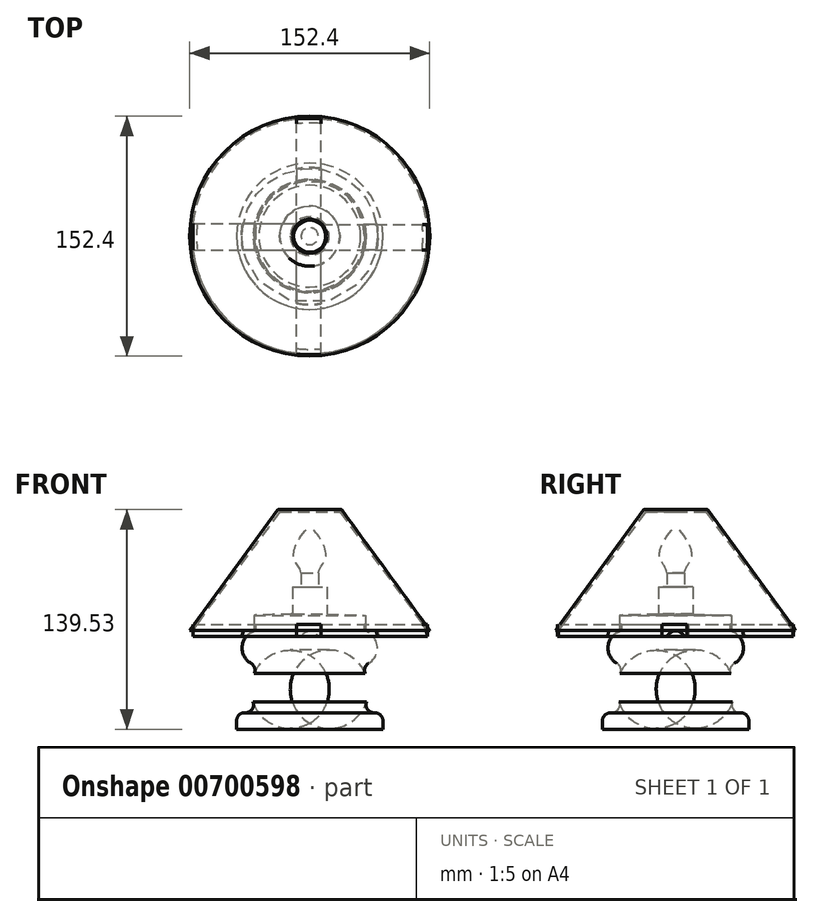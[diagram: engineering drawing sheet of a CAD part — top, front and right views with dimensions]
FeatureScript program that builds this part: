
annotation { "Feature Type Name" : "Feature", "Feature Type Description" : "" }
export const myFeature = defineFeature(function(context is Context, id is Id, definition is map)
    precondition{}
    {
        {
            var Q0;
            Q0=qCreatedBy(makeId("Front.planeOp"),FACE);
            var sketch = newSketch(context, id + "F0", { "sketchPlane" : qUnion([Q0])});
            skLineSegment(sketch, "E0", {"start": v(-76.2, 0) * mm, "end": v(-20.32, 76.66) * mm});
            skLineSegment(sketch, "E1", {"start": v(-20.32, 76.66) * mm, "end": v(0, 77.04) * mm});
            skLineSegment(sketch, "E2", {"start": v(0, 77.04) * mm, "end": v(0, -62.86) * mm});
            skLineSegment(sketch, "E3", {"start": v(0, -62.86) * mm, "end": v(-46.45, -62.86) * mm});
            skLineSegment(sketch, "E4", {"start": v(-46.45, -62.86) * mm, "end": v(-46.45, -52.2) * mm});
            skLineSegment(sketch, "E5", {"start": v(-46.45, -52.2) * mm, "end": v(-32.28, -52.56) * mm});
            skArc(sketch, "E6", {"start": v(-32.28, -22.38) * mm, "mid": v(-37.38, -37.47) * mm, "end": v(-32.28, -52.56) * mm});
            skArc(sketch, "E7", {"start": v(-32.28, 0) * mm, "mid": v(-43, -11.2) * mm, "end": v(-32.28, -22.38) * mm});
            skLineSegment(sketch, "E8", {"start": v(-32.28, 0) * mm, "end": v(-76.2, 0) * mm});
            skSolve(sketch);
        }
        {
            var Q0;
            Q0 = qSketchRegion(id + "F0", true);
            var Q1;
            Q1=sQuery(id+"F0.wireOp",EDGE,"E2");
            revolve(context, id + "F1", {"entities" : qUnion([Q0]), "axis" : qUnion([Q1]), "revolveType" : RevolveType.FULL});
        }
        {
            var Q0;
            Q0=qCreatedBy(makeId("Front.planeOp"),FACE);
            var sketch = newSketch(context, id + "F2", { "sketchPlane" : qUnion([Q0])});
            skLineSegment(sketch, "E9", {"start": v(-19.07, 75.29) * mm, "end": v(-74.68, 0) * mm});
            skLineSegment(sketch, "E10", {"start": v(-74.68, 0) * mm, "end": v(-75.4, -12.03) * mm});
            skLineSegment(sketch, "E11", {"start": v(-75.4, -12.03) * mm, "end": v(-44.38, -11.78) * mm});
            skLineSegment(sketch, "E12", {"start": v(-44.38, -11.78) * mm, "end": v(-43.21, 0) * mm});
            skLineSegment(sketch, "E13", {"start": v(-43.21, 0) * mm, "end": v(-35.55, 0) * mm});
            skLineSegment(sketch, "E14", {"start": v(-35.55, 0) * mm, "end": v(-35.55, 9.61) * mm});
            skLineSegment(sketch, "E15", {"start": v(-35.55, 9.61) * mm, "end": v(-10.84, 10.32) * mm});
            skLineSegment(sketch, "E16", {"start": v(-10.84, 10.32) * mm, "end": v(-10.84, 27.58) * mm});
            skLineSegment(sketch, "E17", {"start": v(-10.84, 27.58) * mm, "end": v(0, 27.58) * mm});
            skLineSegment(sketch, "E18", {"start": v(0, 27.58) * mm, "end": v(0, 27.58) * mm});
            skLineSegment(sketch, "E19", {"start": v(-5.42, 27.58) * mm, "end": v(-5.42, 36.6) * mm});
            skPoint(sketch, "E19.endSnap0", {"position": v(-5.42, 27.58) * mm});
            skFitSpline(sketch, "E20", {"points": [v(-5.42, 36.6) * mm, v(-10.1, 46.56) * mm, v(0, 66.34) * mm], "startDerivative": vector(-6.68, 29.52) * mm, "endDerivative": vector(36.52, 35.64) * mm});
            skLineSegment(sketch, "E21", {"start": v(0, 66.34) * mm, "end": v(0, 27.58) * mm});
            skLineSegment(sketch, "E22", {"start": v(0, 66.34) * mm, "end": v(0, 78.34) * mm});
            skLineSegment(sketch, "E23", {"start": v(0, 78.34) * mm, "end": v(-19.07, 78.4) * mm});
            skLineSegment(sketch, "E24", {"start": v(-19.07, 78.4) * mm, "end": v(-19.07, 75.29) * mm});
            skSolve(sketch);
        }
        {
            var Q0;
            Q0=makeQuery(id+"F2.imprint","IMPRINT",FACE,{"disambiguationData":[TD([[makeQuery(id+"F2.imprint","IMPRINT",EDGE,{"derivedFrom":sQuery(id+"F2.wireOp",EDGE,"E9")}),1.0]])]});
            var Q1;
            Q1=sQuery(id+"F2.wireOp",EDGE,"E21");
            revolve(context, id + "F3", {"operationType" : NewBodyOperationType.REMOVE, "entities" : qUnion([Q0]), "axis" : qUnion([Q1]), "revolveType" : RevolveType.FULL, "oppositeDirection" : true});
        }
        {
            var Q0;
            Q0=makeQuery(id+"F1.opRevolve","SWEPT_EDGE",EDGE,{"disambiguationData":[OSD([sQuery(id+"F0.wireOp",EDGE,"E6"),sQuery(id+"F0.wireOp",EDGE,"E7")])]});
            fillet(context, id + "F4", {"entities" : qUnion([Q0]), "radius" : 5.08 * mm, "tangentPropagation" : true, "allowEdgeOverflow" : false});
        }
        {
            var Q0;
            Q0=qCreatedBy(makeId("Top.planeOp"),FACE);
            var sketch = newSketch(context, id + "F5", { "sketchPlane" : qUnion([Q0])});
            skLineSegment(sketch, "E25.bottom", {"start": v(-74.15, -8.66) * mm, "end": v(0, -8.66) * mm});
            skLineSegment(sketch, "E25.top", {"start": v(-74.15, 8.05) * mm, "end": v(0, 8.05) * mm});
            skLineSegment(sketch, "E25.left", {"start": v(-74.15, -8.66) * mm, "end": v(-74.15, 8.05) * mm});
            skLineSegment(sketch, "E25.right", {"start": v(0, -8.66) * mm, "end": v(0, 8.05) * mm});
            skLineSegment(sketch, "E26.bottom", {"start": v(0, -8.66) * mm, "end": v(74.7, -8.66) * mm});
            skLineSegment(sketch, "E26.top", {"start": v(0, 7.32) * mm, "end": v(74.7, 7.32) * mm});
            skLineSegment(sketch, "E26.left", {"start": v(0, -8.66) * mm, "end": v(0, 7.32) * mm});
            skLineSegment(sketch, "E26.right", {"start": v(74.7, -8.66) * mm, "end": v(74.7, 7.32) * mm});
            skLineSegment(sketch, "E27.bottom", {"start": v(-8.47, -75.16) * mm, "end": v(7.01, -75.16) * mm});
            skLineSegment(sketch, "E27.top", {"start": v(-8.47, 74.7) * mm, "end": v(7.01, 74.7) * mm});
            skLineSegment(sketch, "E27.left", {"start": v(-8.47, -75.16) * mm, "end": v(-8.47, 74.7) * mm});
            skLineSegment(sketch, "E27.right", {"start": v(7.01, -75.16) * mm, "end": v(7.01, 74.7) * mm});
            skSolve(sketch);
        }
        {
            var Q0;
            Q0 = qSketchRegion(id + "F5", true);
            extrude(context, id + "F6", {"entities" : qUnion([Q0]), "endBound" : BoundingType.SYMMETRIC, "oppositeDirection" : true, "depth" : 7.55 * mm, "offsetDistance" : 25.4 * mm});
        }
        {
            var Q0;
            Q0=makeQuery(id+"F1.opRevolve","SWEPT_EDGE",EDGE,{"disambiguationData":[OSD([sQuery(id+"F0.wireOp",EDGE,"E4"),sQuery(id+"F0.wireOp",EDGE,"E5")])]});
            var Q1;
            Q1=makeQuery(id+"F1.opRevolve","SWEPT_EDGE",EDGE,{"disambiguationData":[OSD([sQuery(id+"F0.wireOp",EDGE,"E5"),sQuery(id+"F0.wireOp",EDGE,"E6")])]});
            fillet(context, id + "F7", {"entities" : qUnion([Q0, Q1]), "radius" : 5.08 * mm, "tangentPropagation" : true, "allowEdgeOverflow" : false});
        }
        {
            var Q0;
            Q0=makeQuery(id+"F3.boolean.opBoolean","INTERSECT",EDGE,{"derivedFrom":[makeQuery(id+"F1.opRevolve","SWEPT_FACE",FACE,{"disambiguationData":[OSD([sQuery(id+"F0.wireOp",EDGE,"E1")])]}),makeQuery(id+"F3.opRevolve","SWEPT_FACE",FACE,{"disambiguationData":[OSD([sQuery(id+"F2.wireOp",EDGE,"E24")])]})]});
            var Q1;
            Q1=makeQuery(id+"F1.opRevolve","SWEPT_EDGE",EDGE,{"disambiguationData":[OSD([sQuery(id+"F0.wireOp",EDGE,"E0"),sQuery(id+"F0.wireOp",EDGE,"E1")])]});
            fillet(context, id + "F8", {"entities" : qUnion([Q0, Q1]), "radius" : 0.37 * mm, "tangentPropagation" : true, "allowEdgeOverflow" : false});
        }
    });
